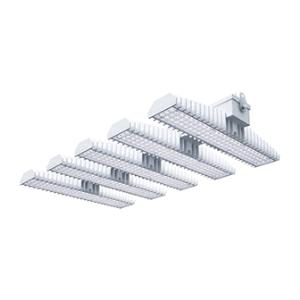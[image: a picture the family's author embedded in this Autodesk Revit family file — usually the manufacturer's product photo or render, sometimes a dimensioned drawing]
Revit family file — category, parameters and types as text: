
# Revit family: 3f_filippi_-_3f_lem_ht_ampio_3f_filippi_-_59030_a0811_-_3f_lem_5_ht_led_150_cr_ampio___vt_0236
name_source: partatom
category: Lighting Fixtures
units: mm (PartAtom-declared; Revit-internal decimal feet)

## family parameters
Cut with Voids When Loaded = No
Host = Face
Light Source = No
Part Type = Normal
Room Calculation Point = No
Round Connector Dimension = Use Diameter
Shared = No

## types (1)
- 3F Filippi - 3F LEM HT Ampio (1 x LED, 25297 lm, 170 W, 4000 K)
    Apparent Load = 170 VA
    Approval mark = ENEC
    CIE Flux Codes = 60 92 99 100 100
    Color Rendering = 80
    Color Temperature = 4000 K
    Control Gear = Electronic ballast
    Default Elevation = 1800 mm
    Description = Industrial luminaire with high light output and high luminous efficiency designed with the most innovative technologies for environments with temperature up to 70°C.

ILLUMINOTECHNICAL
Luminous efficiency 100% (DLOR 99%, ULOR 1%).
Initial luminous flux of the luminaire 25297 lm.
Direct symmetric wide distribution: the illuminated area has a rectangular shape.
Installation Interdistance Transv.D = 1.58 x hu - Long.D = 1.45 x hu.
Tabular UGR (CIE 117 - 4H-8H; S=0.25H; 70/50/20): RUG 21.3 - 22.4.
Beam angle: 93° - 99°.
Luminous efficacy 149 lm/W.
Lifetime (L93/B10): 30000 h. (tq+25°C)
Lifetime (L90/B10): 50000 h. (tq+25°C)
Lifetime (L85/B10): 80000 h. (tq+25°C)
Lifetime (L80/B10): 100000 h. (tq+25°C)
Lifetime (L85/B10): 50000 h. (tq+70°C)
Sudden decreased luminous flux after 50000 hours: 0% (C0).
Photobiological safety in compliance with IEC/TR 62778: RG0 risk exempt, (IEC 62471).
In compliance with IEC/EN 62722-2-1 - IEC/EN 62717 standards.
Luminous flux at +70°C: -13.5%.

SOURCE
5 Mid-Power linear LED modules 30W/840.
Energy efficiency class (UE 2019/2020 - UE 2019/2015): C.
CIE 13.3 Colour rendering index: CRI >80 (R9 <50%).
IES TM-30 Fidelity Index: Rf = 84 Rg = 95.
CCT nominal colour temperature 4000 K.
Colour initial tolerance (MacAdam): SDCM 3.

MECHANICAL
Passive modular heatsinks in die-casted aluminium, painted in white colour.
To optimize the thermal management of the LED module, the heatsinks are oversized and provided with self-cleaning of cooling fins.
Wiring body in aluminium and galvanised steel anchored solidly to the sinks and thermally separated.
3F Lens lenses with high luminous efficiency, transparent polycarbonate, fixed to the LED modules.
Fixing brackets in stainless steel.
Luminaire with limited surface temperature. - D - (EN 60598-2-24)
Dimensions: 952x542 mm, height 133 mm. Weight 23.84 kg.
IP65 protection degree.
Mechanical strength to impacts IK08 (5 joule).
Glow-wire test resistance 850°C.

ELECTRICAL
Halogen Free electronic wiring 230V-50/60Hz, power factor 0.95, THD <25%, constant output current, class I, 2 driver.
Power of the luminaire 170 W.
CE - IEC 60598-1 - EN 60598-1.
SAFE FLICKER: PstLM=<1 and SVM=<0.4 (IEC TR 61547-1 and IEC TR 63158), to ensure a more comfortable and safe light.
Luminaire compliant with EN 60598-2-22 for power supply from a centralised emergency system CPSS (Central Power Supply System), not incorporated in the luminaire - high risk areas excluded. The default power and flux are 100% in AC and 100% in DC.
Ambient temperature from -30°C to +70°C.
Temperature class T6 max 85°C.
Quick connection via M20 3P connector with 9-13 mm tightening range.
Power unit positioned on a separate compartment by the LED module to ensure optimum temperatures of cabling components, to be inspectable and maintainable.
Relative humidity UR: <85%.

INSTALLATION
Ceiling / Suspended / Wall.
All accessories dedicated to this product are available on the Catalog and on our website www.3F-Filippi.com.

ACCESSORIES
A0811 - VT transparent glass, tempered, not flammable, with sealing gasket.
One required for each light module. The pack contains 10 pieces.

APPLICATIONS
In commercial environments, exhibition and industrial areas, stores, open areas.
Applications with high ambient temperature up to 70°C.

WARNING
Fixture not suitable for cold stores with an ambient temperature <0°C and/or relative humidity >85%.
Luminaire designed for disposal/recycling at end-of-life.
Replaceable (LED only) light source by a professional. Replaceable control gear by a professional.
    Height = 133 mm  [stored 0.436352 ft]
    Lamp = 1 x LED
    Lamp Light Flux = 25297 lm
    Lamp Power = 170 W
    Lamp count = 1
    Length = 952 mm
    Lifetime = 50000 h
    Luminous efficacy = 149 lm/W
    Manufacturer = 3F Filippi
    ModVariant = No
    Model = 3F Filippi - 59030+A0811 - 3F LEM 5 HT LED 150 CR AMPIO + VT
    Mounting Place = Ceiling
    Mounting Type = Pendant
    Number of Poles = 1
    OnlyDefault = Yes
    Power Factor = 1
    Product Name = 3F Filippi - 3F LEM HT Ampio
    Product group = pendant luminaire
    ProductGroupID = 9
    Protection Class = Protection class I
    Protection Degree = IP 65
    RLX_Detail_Level = 1
    RLX_Emergency_Light_Flux = 0 lm
    RLX_Emergency_Type = 0
    RLX_Emergency_Type_DB = No
    RlxData = <blob elided: 125957 chars, md5=8ae770ad>
    Socket = socket
    Standby Power = 0 W
    System Light Flux = 25297 lm
    System Power = 170 W
    Type Comments = Product without accessories
    Type Image = 3f_filippi_-_lem_5__a0811.jpg
    URL = http://relux.com
    VarID = ---
    Voltage = 0 V
    Weight = 0.00 kg
    Width = 542 mm

note: [stored X ft] marks values corroborated as IEEE doubles in the binary element streams (Revit-internal decimal feet)

## geometry (parser evidence)
native form markers: Blend x4, Sweep x15
no freeform markers — native parametric forms only
